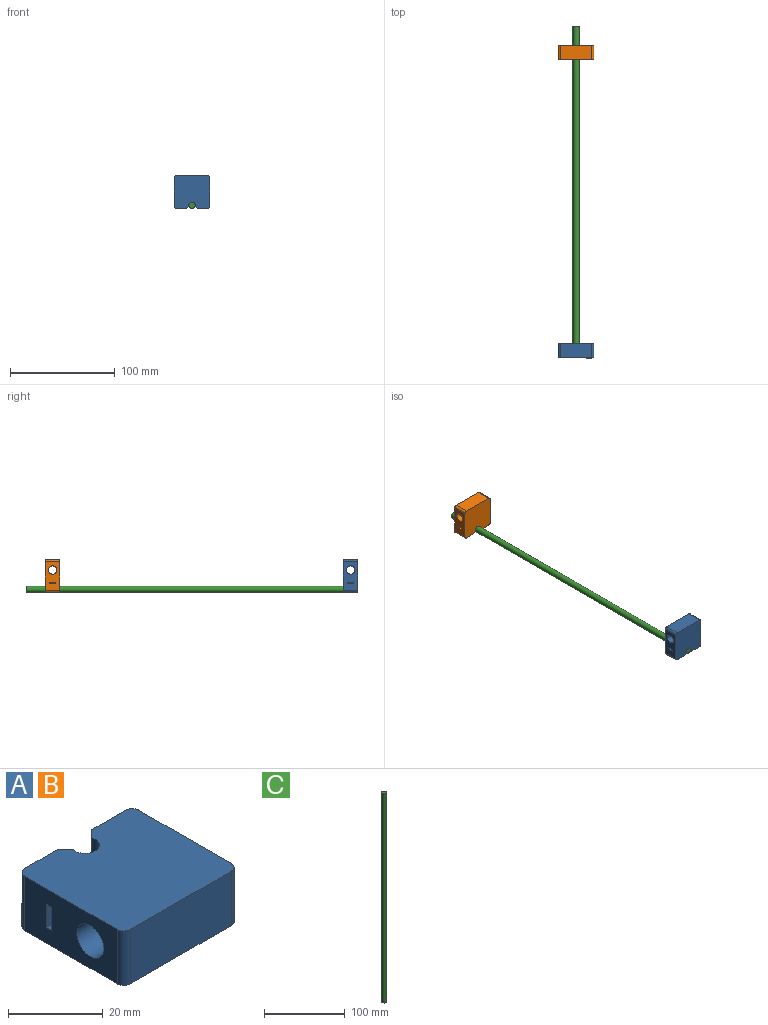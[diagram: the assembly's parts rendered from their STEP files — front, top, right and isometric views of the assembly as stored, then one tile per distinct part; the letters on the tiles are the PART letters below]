
ASSEMBLY  parts=3 mates=1
PART A: 19 faces, bbox 34x31.5x14 mm
  f0: plane 27.5x14mm, normal (1,0,0), area 325.7mm2, adj f3,f7,f10,f11,f12,f13,f14,f15
  f1: plane 27.5x14mm, normal (-1,0,0), area 325.7mm2, adj f3,f7,f10,f11,f12,f13,f14,f16
  f2: plane 14x10mm, normal (0,1,0), area 140mm2, adj f3,f7,f9,f16
  f3: plane 34x31.5mm, normal (0,0,1), area 1031.5mm2, adj f0,f1,f2,f4,f5,f6,f8,f9
  f4: cylinder r=3mm len=14mm, axis (0,0,-1), area 156.7mm2, adj f3,f7,f8,f9
  f5: plane 14x10mm, normal (0,1,0), area 140mm2, adj f3,f7,f8,f15
  f6: plane 30x14mm, normal (0,-1,0), area 420mm2, adj f3,f7,f17,f18
  f7: plane 34x31.5mm, normal (0,0,-1), area 1031.5mm2, adj f0,f1,f2,f4,f5,f6,f8,f9
  f8: plane 14x2.13mm, normal (-0.71,0.71,0), area 42.2mm2, adj f3,f4,f5,f7
  f9: plane 14x2.13mm, normal (0.71,0.71,0), area 42.2mm2, adj f2,f3,f4,f7
  f10: plane 34x6mm, normal (0,-1,0), area 204mm2, adj f0,f1,f11,f13
  f11: plane 34x1.5mm, normal (0,0,-1), area 51mm2, adj f0,f1,f10,f12
  f12: plane 34x6mm, normal (0,1,0), area 204mm2, adj f0,f1,f11,f13
  f13: plane 34x1.5mm, normal (0,0,1), area 51mm2, adj f0,f1,f10,f12
  f14: cylinder r=4mm len=34mm, axis (1,0,0), area 854.5mm2, adj f0,f1
  f15: cylinder r=2mm len=14mm, axis (0,0,1), area 44mm2, adj f0,f3,f5,f7
  f16: cylinder r=2mm len=14mm, axis (0,0,-1), area 44mm2, adj f1,f2,f3,f7
  f17: cylinder r=2mm len=14mm, axis (0,0,1), area 44mm2, adj f1,f3,f6,f7
  f18: cylinder r=2mm len=14mm, axis (0,0,-1), area 44mm2, adj f0,f3,f6,f7
PART B: same geometry as A
PART C: 3 faces, bbox 6x6x317.5 mm
  f0: cylinder r=3mm len=317.5mm, axis (0,0,-1), area 5984.7mm2, adj f1,f2
  f1: plane 6x6mm, normal (0,0,1), area 28.3mm2, adj f0
  f2: plane 6x6mm, normal (0,0,-1), area 28.3mm2, adj f0
PLACE A rot(axis=(-1,0,0),90deg) t=(-161.53,-77.83,186)mm
PLACE B rot(axis=(-1,0,0),90deg) t=(-161.53,207.17,186)mm
PLACE C rot(axis=(-1,0,0),90deg) t=(-161.53,-77.83,173.25)mm
MATE planar C.f0 <-> A.f4  axis (0,-1,0) through (-161.53,-77.83,173.25)mm
